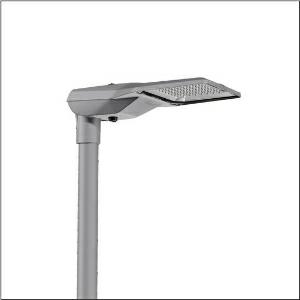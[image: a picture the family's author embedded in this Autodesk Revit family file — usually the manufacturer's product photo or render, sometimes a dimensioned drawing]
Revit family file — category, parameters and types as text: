
# Revit family: streetlight_sl_21_iq_midi___st0_5a_5xe3b31y08mb_2f18
name_source: partatom
category: Lighting Fixtures
units: mm (PartAtom-declared; Revit-internal decimal feet)

## family parameters
Cut with Voids When Loaded = No
Host = Face
Light Source = No
Part Type = Normal
Room Calculation Point = No
Round Connector Dimension = Use Diameter
Shared = No

## types (1)
- --- (1 x LED, 18340 lm, 129.3 W, 3000K)
    Apparent Load = 129 VA
    CIE Flux Codes = 41 75 97 100 100
    Color Rendering = 70
    Color Temperature = 3000K
    Default Elevation = 1800 mm
    Description = Streetlight SL 21 iQ midi, mast luminaire, primary light control with lens, of PMMA, primary optical cover: cover, of toughened safety glass, transparent, light distribution: ST0.5a, light emission: direct distribution, primary light characteristic: asymmetric, installation type: post-top, side-entry, LED, High Power LED, rated luminous flux: 18.340lm, luminous efficacy: 142lm/W, light colour: 730, colour temperature: 3000K, control gear: iQ-Street Remote, D4i with power reduction, control: pre-setting: logarithmic dimming characteristic, Street-Remote, Auto-Match, Temp-Guard, Lumen-Switch, Night-Set, Smart-Wire, Light-Fading, Desk-Remote (wireless, voltage-free reading and setting of iQ features in the workshop via application-optimized NFC function/RFID function), optimised constant luminous flux control (CLO 2.0), mains connection: 230..240V, AC, 50/60Hz, start of lifetime: 129W, end of service life: 142W, reduction: 56W, luminaire housing, of diecast aluminium, powder-coated, SITECO metallic grey (DB 702S), corrosivity category C5 high according to DIN EN ISO 12944, please order mast flange separately, inclination adjustable: 0°, 5°, 10°, 15°, sealing non-destructively replaceable, multi-level sealing system, length: 644mm, width: 335mm, height: 110mm, mast flange for spigot size: 42mm (side-entry): 5XC10008XM4, 60/48mm (side-entry/post-top): 5XC10108XM2, 76/60mm (side-entry/post-top): 5XC10108XM1, mounting height: 4..8m, Smart Interface below and above, protection rating (complete): IP66, insulation class (complete): insulation class II (safety insulation), certification: CE, ENEC, ENEC+, VDE, impact resistance: IK10, permissible operating ambient temperature for outdoor applications: -40..+50°C, standard-compliant lighting for roads and squares, packaging unit: 1 piece

Light Distribution: ST0.5a
    Height = 111 mm
    Lamp = 1 x LED
    Lamp Light Flux = 18340 lm
    Lamp Power = 129.3 W
    Lamp count = 1
    Length = 644 mm
    Luminous efficacy = 142 lm/W
    Manufacturer = Siteco
    ModVariant = No
    Model = 5XE3B31Y08MB
    Number of Poles = 1
    OnlyDefault = Yes
    Power Factor = 1
    Product Name = Streetlight SL 21 iQ midi | ST0.5a
    Product group = mast luminaire | pylon top
    ProductGroupID = 6100
    Protection Class = Protection class II
    Protection Degree = IP 66
    RLX_Detail_Level = 1
    RLX_Emergency_Light_Flux = 0 lm
    RLX_Emergency_Type = 0
    RLX_Emergency_Type_DB = No
    RlxData = <blob elided: 102169 chars, md5=f3631990>
    Socket = socket
    Standby Power = 0 W
    System Light Flux = 18340 lm
    System Power = 129 W
    Type Comments = factory setting: luminous flux: 100 % | dim-lin: 254 | 672 mA
    Type Image = l_1004304.jpg
    URL = http://relux.com
    VarID = @adj_116189
    Voltage = 0 V
    Weight = 0.00 kg
    Width = 336 mm

## geometry (parser evidence)
native form markers: Blend x4, Sweep x11
no freeform markers — native parametric forms only
